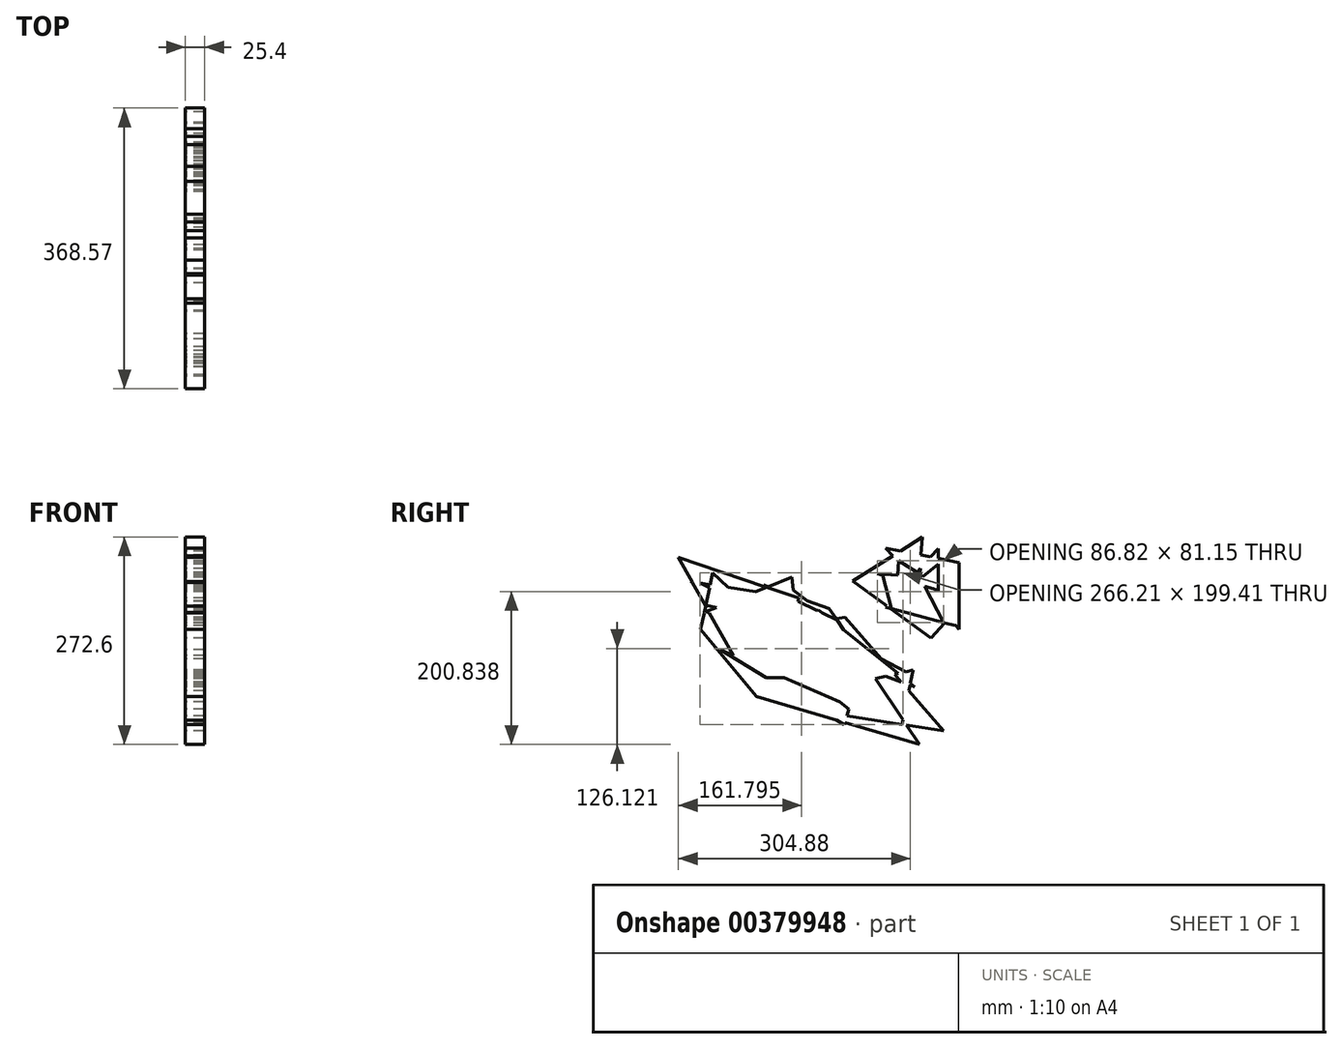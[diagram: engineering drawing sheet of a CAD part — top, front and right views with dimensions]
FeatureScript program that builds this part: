
annotation { "Feature Type Name" : "Feature", "Feature Type Description" : "" }
export const myFeature = defineFeature(function(context is Context, id is Id, definition is map)
    precondition{}
    {
        {
            var Q0;
            Q0=qCreatedBy(makeId("Right.planeOp"),FACE);
            var sketch = newSketch(context, id + "F0", { "sketchPlane" : qUnion([Q0])});
            skLineSegment(sketch, "E0", {"start": v(33.13, 13.44) * mm, "end": v(-14.28, -12.65) * mm});
            skLineSegment(sketch, "E1", {"start": v(-61.68, 32.82) * mm, "end": v(151.92, -78.6) * mm});
            skLineSegment(sketch, "E2", {"start": v(-32.56, 49.58) * mm, "end": v(14.85, -48.64) * mm});
            skLineSegment(sketch, "E3", {"start": v(63.4, 0) * mm, "end": v(-56.54, -22.18) * mm});
            skLineSegment(sketch, "E4", {"start": v(-99.38, 28.59) * mm, "end": v(49.69, -49.9) * mm});
            skLineSegment(sketch, "E5", {"start": v(-9.7, 51.68) * mm, "end": v(0, -30.34) * mm});
            skLineSegment(sketch, "E6", {"start": v(-58.83, 21.83) * mm, "end": v(52.84, -36.97) * mm});
            skLineSegment(sketch, "E7", {"start": v(0, 41.83) * mm, "end": v(-6.85, -59.56) * mm});
            skLineSegment(sketch, "E8", {"start": v(-46.83, 41.88) * mm, "end": v(85.1, -21.78) * mm});
            skLineSegment(sketch, "E9", {"start": v(-130.8, 44.3) * mm, "end": v(-22.85, -9.02) * mm});
            skLineSegment(sketch, "E10", {"start": v(-167.92, 24.93) * mm, "end": v(4, -43.55) * mm});
            skLineSegment(sketch, "E11", {"start": v(-37.7, 27.42) * mm, "end": v(-16.56, -59.65) * mm});
            skLineSegment(sketch, "E12", {"start": v(-112.42, 2.83) * mm, "end": v(167.35, -97.85) * mm});
            skLineSegment(sketch, "E13", {"start": v(-71.96, 51.15) * mm, "end": v(-20.56, -61.93) * mm});
            skLineSegment(sketch, "E14", {"start": v(-228.46, 87.19) * mm, "end": v(87.96, -64.42) * mm});
            skLineSegment(sketch, "E15", {"start": v(-43.4, 34.56) * mm, "end": v(-20, -64.86) * mm});
            skLineSegment(sketch, "E16", {"start": v(-130.8, 7.03) * mm, "end": v(121.65, -87.54) * mm});
            skLineSegment(sketch, "E17", {"start": v(-8.85, 0.47) * mm, "end": v(97.67, -86.75) * mm});
            skLineSegment(sketch, "E18", {"start": v(164.49, -67.08) * mm, "end": v(16.56, -99.62) * mm});
            skLineSegment(sketch, "E19", {"start": v(-93.1, 11.6) * mm, "end": v(89.95, -54.28) * mm});
            skLineSegment(sketch, "E20", {"start": v(-113.66, 57.82) * mm, "end": v(47.4, -97.9) * mm});
            skLineSegment(sketch, "E21", {"start": v(-46.83, 41.88) * mm, "end": v(27.41, -65.48) * mm});
            skLineSegment(sketch, "E22", {"start": v(65.11, -24.97) * mm, "end": v(-142.79, 19.3) * mm});
            skLineSegment(sketch, "E23", {"start": v(-113.66, 52.21) * mm, "end": v(-50.83, -71.53) * mm});
            skLineSegment(sketch, "E24", {"start": v(-78.82, 18.96) * mm, "end": v(-55.4, -29.35) * mm});
            skLineSegment(sketch, "E25", {"start": v(20.56, -17.54) * mm, "end": v(-118.23, -8.82) * mm});
            skLineSegment(sketch, "E26", {"start": v(7.3, -59.12) * mm, "end": v(77.1, -78.45) * mm});
            skLineSegment(sketch, "E27", {"start": v(-25.7, -55.08) * mm, "end": v(-139.36, -13.42) * mm});
            skLineSegment(sketch, "E28", {"start": v(-48.83, -13.18) * mm, "end": v(-74.25, -93.13) * mm});
            skLineSegment(sketch, "E29", {"start": v(-110.23, -29.96) * mm, "end": v(31.98, -82.93) * mm});
            skLineSegment(sketch, "E30", {"start": v(-72, -11.72) * mm, "end": v(122.23, -167.3) * mm});
            skLineSegment(sketch, "E31", {"start": v(54.83, -80.18) * mm, "end": v(-43.4, -80.18) * mm});
            skLineSegment(sketch, "E32", {"start": v(-103.95, -43.65) * mm, "end": v(98.8, -131.84) * mm});
            skLineSegment(sketch, "E33", {"start": v(99.38, -14.74) * mm, "end": v(57.88, -145.29) * mm});
            skLineSegment(sketch, "E34", {"start": v(-38.27, 59.36) * mm, "end": v(191.9, -124.31) * mm});
            skLineSegment(sketch, "E35", {"start": v(-126.03, 5.25) * mm, "end": v(-9.7, 51.68) * mm});
            skLineSegment(sketch, "E36", {"start": v(-170.2, 98.3) * mm, "end": v(-81.67, -60.07) * mm});
            skLineSegment(sketch, "E37", {"start": v(-165.63, 49.58) * mm, "end": v(-1.22, 23.74) * mm});
            skLineSegment(sketch, "E38", {"start": v(-179.34, 85.05) * mm, "end": v(57.11, 4.75) * mm});
            skLineSegment(sketch, "E39", {"start": v(26.84, 29.78) * mm, "end": v(187.9, -213.98) * mm});
            skLineSegment(sketch, "E40", {"start": v(34.84, -125.9) * mm, "end": v(213.9, -154.05) * mm});
            skLineSegment(sketch, "E41", {"start": v(-103.95, -43.65) * mm, "end": v(58.97, -141.87) * mm});
            skLineSegment(sketch, "E42", {"start": v(-74.25, -99.62) * mm, "end": v(173.06, -172.6) * mm});
            skLineSegment(sketch, "E43", {"start": v(-139.36, -5.55) * mm, "end": v(-43.4, -120.18) * mm});
            skLineSegment(sketch, "E44", {"start": v(-113.66, 57.82) * mm, "end": v(-131.43, -25.65) * mm});
            skLineSegment(sketch, "E45", {"start": v(59.97, -0.63) * mm, "end": v(197.62, -159.15) * mm});
            skLineSegment(sketch, "E46", {"start": v(152.67, -56.05) * mm, "end": v(134.66, -141.6) * mm});
            skSolve(sketch);
        }
        {
            var Q0;
            Q0 = qSketchRegion(id + "F0", true);
            extrude(context, id + "F1", {"entities" : qUnion([Q0]), "depth" : 25.4 * mm});
        }
        {
            var Q0;
            Q0=qCreatedBy(makeId("Right.planeOp"),FACE);
            var sketch = newSketch(context, id + "F2", { "sketchPlane" : qUnion([Q0])});
            skLineSegment(sketch, "E47", {"start": v(182.63, 39.6) * mm, "end": v(126.93, 75.9) * mm});
            skLineSegment(sketch, "E48", {"start": v(209.64, 90.24) * mm, "end": v(147.19, 40.45) * mm});
            skLineSegment(sketch, "E49", {"start": v(222.3, 45.51) * mm, "end": v(94.02, 57.33) * mm});
            skLineSegment(sketch, "E50", {"start": v(161.53, 104.59) * mm, "end": v(158.16, 51.42) * mm});
            skLineSegment(sketch, "E51", {"start": v(204.58, 22.73) * mm, "end": v(121.02, 64.92) * mm});
            skLineSegment(sketch, "E52", {"start": v(132, 86.87) * mm, "end": v(126.06, 22.43) * mm});
            skLineSegment(sketch, "E53", {"start": v(223.99, 68.3) * mm, "end": v(113.43, 90.24) * mm});
            skLineSegment(sketch, "E54", {"start": v(209.64, 79.27) * mm, "end": v(209.64, -16.94) * mm});
            skPoint(sketch, "E54.startSnap0", {"position": v(168.7, 79.27) * mm});
            skLineSegment(sketch, "E55", {"start": v(229.9, 22.73) * mm, "end": v(102.54, 56.54) * mm});
            skLineSegment(sketch, "E56", {"start": v(182.63, 122.31) * mm, "end": v(182.63, 22.73) * mm});
            skLineSegment(sketch, "E57", {"start": v(113.43, 90.24) * mm, "end": v(209.64, -16.94) * mm});
            skLineSegment(sketch, "E58", {"start": v(223.99, -16.94) * mm, "end": v(113.43, 12.42) * mm});
            skLineSegment(sketch, "E59", {"start": v(101.61, 86.87) * mm, "end": v(123.56, 0) * mm});
            skLineSegment(sketch, "E60", {"start": v(161.53, 104.59) * mm, "end": v(48.44, 32.85) * mm});
            skLineSegment(sketch, "E61", {"start": v(189.36, -7.75) * mm, "end": v(132, 104.59) * mm});
            skLineSegment(sketch, "E62", {"start": v(196.14, 104.59) * mm, "end": v(113.43, 12.42) * mm});
            skLineSegment(sketch, "E63", {"start": v(52.66, 59.02) * mm, "end": v(191.92, -41.42) * mm});
            skLineSegment(sketch, "E64", {"start": v(98.24, 115.56) * mm, "end": v(102.54, 23.04) * mm});
            skLineSegment(sketch, "E65", {"start": v(209.64, 12.42) * mm, "end": v(161.53, -41.2) * mm});
            skSolve(sketch);
        }
        {
            var Q0;
            Q0 = qSketchRegion(id + "F2", true);
            extrude(context, id + "F3", {"entities" : qUnion([Q0]), "depth" : 25.4 * mm});
        }
    });
